# Revit family: PS1408
name_source: partatom
category: Luminarias
units: mm (PartAtom-declared; Revit-internal decimal feet)

## family parameters
Compartido = Sí
Corte con vacíos al cargar = No
Cota de conector redondo = Diámetro de uso
Origen de luz = No
Punto de cálculo de habitación = No
Se basa en plano de trabajo = Sí
Siempre vertical = No
Tipo de pieza = Normal

## types (1)
- PERFIL_PS1408
    Clips de Sujecion 1408.2 = 3
    Descripción = PERFIL DE ALUMINIO CON DIFUSOR LECHOSO, PARA ALOJAR HASTA DOS TIRAS LUMINOSAS (DEPENDIENDO EL MODELO), PERFIL DE COLOCACION DE 11MM DE ANCHO. INSTALACION SOBRE SUPERFICIES PLANAS, PERFIL DE SOBREPONER. IDEAL PARA ATENUAR EL BRILLO E INCORPORAR LA LUZ AL AMBIENTE.PRESENTACION DESDE 0.5 - 3 METROS, REQUEIRE ACCESORIOS COMO TAPA FINAL (CONSIDERAR 1 POR SEGMENTO DE PERFIL), CLIPS DE SUJECION LINEAL (CONSIDERAR 3 PZAS POR SEGMENTO DE PERFIL).
    Elevación por defecto = 1219 mm
    Fabricante = BRILLANT
    Longitud = 1200 mm
    Modelo = PS1408
    Tapa Final 1408.1 = 1

## geometry (parser evidence)
native form markers: Blend x2
no freeform markers — native parametric forms only
